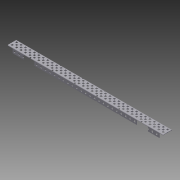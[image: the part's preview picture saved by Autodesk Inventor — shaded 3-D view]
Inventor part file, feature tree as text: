
AUTODESK INVENTOR PART (.ipt)
format: ipt  version: 2012 (Build 160160000, 160)  size: 2,263,552 bytes
history: native  units: in
note: dims shown in document units (in); Inventor stores cm internally (conversion verified against a paired STEP export)
features: extrude x7, sketch x7, other x1, imported_body x1
ambient origin geometry x8: Origin, YZ Plane, XZ Plane, XY Plane, X Axis, Y Axis, Z Axis, Center Point
feature tree (16):
  parser-record x1  (decoder bookkeeping rows leaked as tree rows — omitted from the tree; the rows remain in map.json)
  imported_body  "Base1"
  extrude  "Extrusion1"  Depth=1.0in TaperAngle=0.0deg
  extrude  "Extrusion2"  Depth=1.0in TaperAngle=0.0deg
  extrude  "Extrusion3"  Depth=1.0in TaperAngle=0.0deg
  extrude  "Extrusion4"  [1 undecoded]
  extrude  "Extrusion5"  [1 undecoded]
  extrude  "Extrusion6"  [1 undecoded]
  extrude  "Extrusion7"  [1 undecoded]
  sketch  "Sketch1"  dims[d0=1.0in d1=0.0in d2=1.0in d3=0.0in]
  sketch  "Sketch2"  dims[d4=1.0in d5=0.0in d6=1.0in d7=0.0in]
  sketch  "Sketch3"  dims[d8=1.0in d9=0.0in d10=1.0in d11=0.0in]
  sketch  "Sketch4"  dims[d12=0.5in d13=0.0in]
  sketch  "Sketch5"
  sketch  "Sketch6"
  sketch  "Sketch7"
note: 4 required parameter values undecoded (feature->parameter linkage not recoverable at this tier; creation-order binding heuristic only, values carry confidence <= 0.55)
